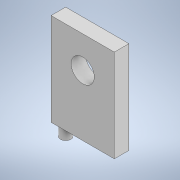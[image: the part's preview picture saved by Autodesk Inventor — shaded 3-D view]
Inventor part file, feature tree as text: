
AUTODESK INVENTOR PART (.ipt)
format: ipt  version: 2021 (Build 250183000, 183)  size: 157,184 bytes
history: native  units: in
note: dims shown in document units (in); Inventor stores cm internally (conversion verified against a paired STEP export)
features: sketch x11, extrude x10
ambient origin geometry x8: Origin, YZ Plane, XZ Plane, XY Plane, X Axis, Y Axis, Z Axis, Center Point
bodies: Body1 (feature_tree)
feature tree (21):
  extrude  "Extrusion9"  Depth=5.1181in
  extrude  "Extrusion10"  Depth=1.1811in
  sketch  "Sketch11"  dims[d37=1.5748in d38=0.0in d39=1.5748in d40=0.0in]
  extrude  "Extrusion11"  Depth=1.5748in TaperAngle=0.0deg
  extrude  "Extrusion12"  Depth=1.5748in TaperAngle=0.0deg
  extrude  "Extrusion14"  Depth=0.3937in TaperAngle=0.0deg
  extrude  "Extrusion15"  Depth=0.5906in
  extrude  "Extrusion16"  Depth=0.9843in TaperAngle=0.0deg
  extrude  "Extrusion18"  Depth=0.9843in
  extrude  "Extrusion19"  Depth=0.5906in
  extrude  "Extrusion20"  Depth=0.9843in
  sketch  "Sketch9"  dims[d32=5.1181in d33=5.1181in]
  sketch  "Sketch10"  dims[d34=1.1811in d35=0.0in d36=1.875in]
  sketch  "Sketch12"  dims[d41=0.7874in d42=0.0in d50=1.5748in d51=0.0in]
  sketch  "Sketch13"  dims[d52=0.5906in d53=0.0in d54=0.3937in d55=0.0in]
  sketch  "Sketch15"  dims[d64=0.8411in d65=0.5906in]
  sketch  "Sketch16"  dims[d66=0.9843in d67=0.5906in d68=0.0in]
  sketch  "Sketch17"  dims[d69=0.9843in d70=0.0in d71=0.8411in]
  sketch  "Sketch19"  dims[d72=0.5906in d73=0.5906in]
  sketch  "Sketch20"  dims[d74=0.9843in d75=0.0in d5=0.0197in]
  sketch  "Sketch21"  dims[d6=0.0344in d7=0.0197in d8=0.0344in d59=0.0197in d60=0.0344in d61=0.0197in d62=0.0344in]
